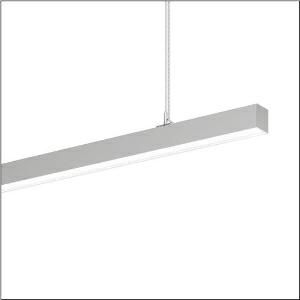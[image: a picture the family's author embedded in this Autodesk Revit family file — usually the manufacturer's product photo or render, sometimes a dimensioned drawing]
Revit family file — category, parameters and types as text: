
# Revit family: silica_r__21_51mx33db39sb_b1fc
name_source: partatom
category: Lighting Fixtures
units: mm (PartAtom-declared; Revit-internal decimal feet)

## family parameters
Cut with Voids When Loaded = No
Host = Face
Light Source = No
Part Type = Normal
Room Calculation Point = No
Round Connector Dimension = Use Diameter
Shared = No

## types (1)
- --- (1 x LED, 7390 lm, 51.6 W, 3000K)
    Apparent Load = 52 VA
    CIE Flux Codes = 78 96 99 55 100
    Color Rendering = 80
    Color Temperature = 3000K
    Default Elevation = 1800 mm
    Description = Silica® 21, office luminaire, primary optical cover: prismatic diffuser, of PMMA, CAT 2 (L<= 3000cd/m²), light emission: direct/indirect distribution, primary light characteristic: symmetric, installation type: suspended mounting, LED, rated luminous flux: 7.390lm, luminous efficacy: 143lm/W, light colour: 830, colour temperature: 3000K, with terminal, 3+2-pole, max. 2.5mm², mains connection: 220..240V, AC, 50/60Hz, rated input power: 51.6W, luminaire housing, of aluminium, metallic grey (RAL 9006), length: 1.504mm, width: 53mm, height: 53mm, protection rating (complete): IP20, insulation class (complete): insulation class I (protective earthing), certification: CE, permissible operating ambient temperature: 0..+35°C, standard: EN 50419, packaging unit: 1 piece
    Height = 53 mm
    Lamp = 1 x LED
    Lamp Light Flux = 7390 lm
    Lamp Power = 51.6 W
    Lamp count = 1
    Length = 1504 mm
    Luminous efficacy = 143 lm/W
    Manufacturer = Siteco
    ModVariant = No
    Model = 51MX33DB39SB
    Mounting Place = Ceiling
    Mounting Type = Pendant
    Number of Poles = 1
    OnlyDefault = Yes
    Power Factor = 1
    Product Name = Silica® 21
    Product group = office luminaire | ceiling pendant
    ProductGroupID = 902
    Protection Class = Protection class I
    Protection Degree = IP 20
    RLX_Detail_Level = 1
    RLX_Emergency_Light_Flux = 0 lm
    RLX_Emergency_Type = 0
    RLX_Emergency_Type_DB = No
    RlxData = <blob elided: 23497 chars, md5=172d232d>
    Socket = socket
    Standby Power = 0 W
    System Light Flux = 7390 lm
    System Power = 52 W
    Type Comments = factory setting: luminous flux: 100 % | dim-lin: 254 | 345 mA
    Type Image = l_1335864.jpg
    URL = http://relux.com
    VarID = @adj_087461
    Voltage = 0 V
    Weight = 0.00 kg
    Width = 53 mm

## geometry (parser evidence)
native form markers: Blend x4, Sweep x12
no freeform markers — native parametric forms only
